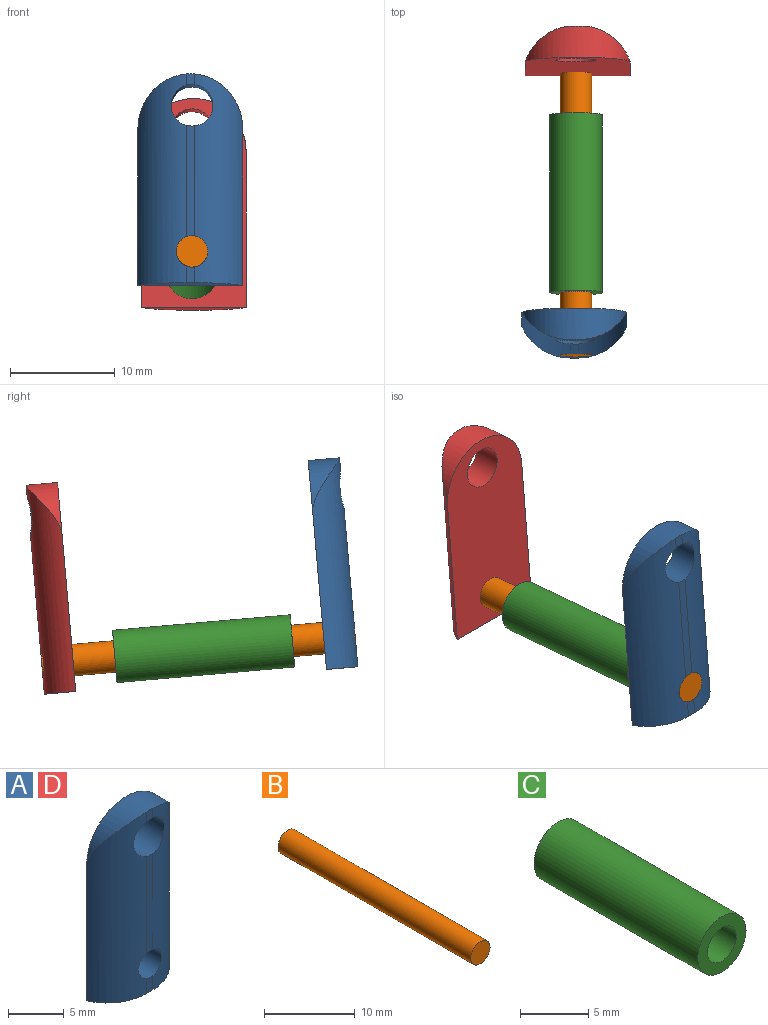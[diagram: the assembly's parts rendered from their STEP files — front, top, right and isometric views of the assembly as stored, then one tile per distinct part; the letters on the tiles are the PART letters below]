
ASSEMBLY  parts=4 mates=3
PART A: 10 faces, bbox 10x3x20 mm
  f0: plane 1.61x0.84mm, normal (0,-1,0), area 1.3mm2, adj f2,f5,f7,f8
  f1: plane 10.7x0.84mm, normal (0,-1,0), area 8.8mm2, adj f5,f6,f7,f8
  f2: plane 10x3mm, normal (0,0,-1), area 22.3mm2, adj f0,f4,f7,f8
  f3: plane 1.08x0.84mm, normal (0,-1,0), area 0.8mm2, adj f6,f7,f8,f9
  f4: plane 20x10mm, normal (0,1,0), area 169.6mm2, adj f2,f5,f6,f7,f8,f9
  f5: cylinder r=1.5mm len=3mm, axis (0,-1,0), area 27.8mm2, adj f0,f1,f4,f7,f8
  f6: cylinder r=2mm len=4mm, axis (0,-1,0), area 36.3mm2, adj f1,f3,f4,f7,f8
  f7: cylinder r=5mm len=19.98mm, axis (0,0,1), area 101.5mm2, adj f0,f1,f2,f3,f4,f5,f6,f9
  f8: cylinder r=5mm len=19.98mm, axis (0,0,-1), area 99.4mm2, adj f0,f1,f2,f3,f4,f5,f6,f9
  f9: cylinder r=5mm len=10mm, axis (0,1,0), area 27.1mm2, adj f3,f4,f7,f8
PART B: 3 faces, bbox 3x30x3 mm
  f0: cylinder r=1.5mm len=30mm, axis (0,1,0), area 282.7mm2, adj f1,f2
  f1: plane 3x3mm, normal (0,-1,0), area 7.1mm2, adj f0
  f2: plane 3x3mm, normal (0,1,0), area 7.1mm2, adj f0
PART C: 4 faces, bbox 5x17x5 mm
  f0: cylinder r=1.5mm len=17mm, axis (0,1,0), area 160.2mm2, adj f2,f3
  f1: cylinder r=2.5mm len=17mm, axis (0,1,0), area 267mm2, adj f2,f3
  f2: plane 5x5mm, normal (0,-1,0), area 12.6mm2, adj f0,f1
  f3: plane 5x5mm, normal (0,1,0), area 12.6mm2, adj f0,f1
PART D: same geometry as A
PLACE A rot(axis=(-1,0,0),5deg) t=(-4.72,-17.9,8.22)mm
PLACE B rot(axis=(-1,0,0),5deg) t=(-4.72,8.4,-0.96)mm
PLACE C rot(axis=(-1,0,0),5deg) t=(-4.72,1.42,-0.35)mm
PLACE D rot(axis=(0,-0.04,-1),180deg) t=(-4.72,6,6.13)mm
MATE fastened D.f5 <-> B.f0  axis (0,1,-0.09) through (-4.72,8.4,-0.96)mm
MATE fastened A.f5 <-> B.f0  axis (0,-1,0.09) through (-4.72,-21.49,1.65)mm
MATE slider C.f0 <-> B.f0  axis (0,1,-0.09) through (-4.72,-7.04,0.39)mm
